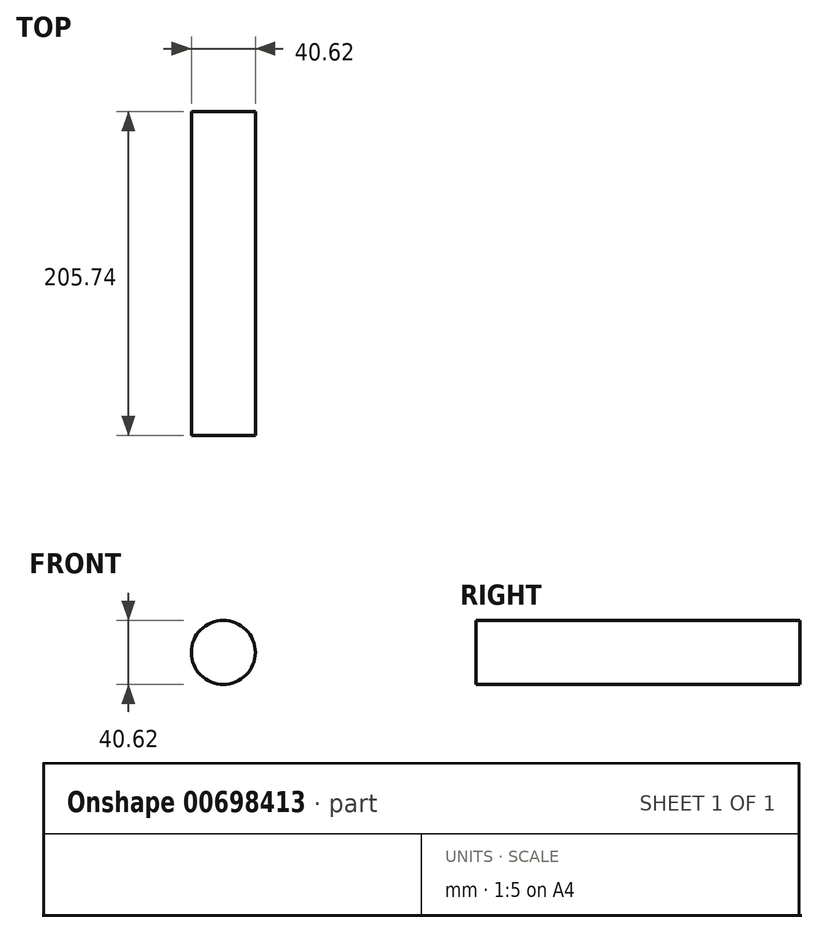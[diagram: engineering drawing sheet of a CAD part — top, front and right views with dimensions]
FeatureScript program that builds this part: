
annotation { "Feature Type Name" : "Feature", "Feature Type Description" : "" }
export const myFeature = defineFeature(function(context is Context, id is Id, definition is map)
    precondition{}
    {
        {
            var Q0;
            Q0=qCreatedBy(makeId("Front.planeOp"),FACE);
            var sketch = newSketch(context, id + "F0", { "sketchPlane" : qUnion([Q0])});
            skCircle(sketch, "E0", {"center": v(0, 0) * mm, "radius": 20.31 * mm});
            skSolve(sketch);
        }
        {
            var Q0;
            Q0=makeQuery(id+"F0.imprint","IMPRINT",FACE,{"disambiguationData":[TD([[makeQuery(id+"F0.imprint","IMPRINT",EDGE,{"derivedFrom":sQuery(id+"F0.wireOp",EDGE,"E0")}),1.0]])]});
            extrude(context, id + "F1", {"entities" : qUnion([Q0]), "depth" : 205.74 * mm, "offsetDistance" : 25.4 * mm});
        }
    });
